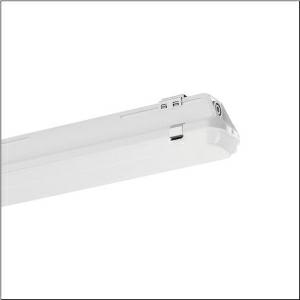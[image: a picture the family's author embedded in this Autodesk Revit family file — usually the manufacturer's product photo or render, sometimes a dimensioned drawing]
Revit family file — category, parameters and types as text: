
# Revit family: monsun_r__12_parking_51fg207p440h_4e28
name_source: partatom
category: Lighting Fixtures
units: mm (PartAtom-declared; Revit-internal decimal feet)

## family parameters
Cut with Voids When Loaded = No
Host = Face
Light Source = No
Part Type = Normal
Room Calculation Point = No
Round Connector Dimension = Use Diameter
Shared = No

## types (1)
- Monsun® 12 parking (1 x LED, 4820 lm, 29.2 W, 4000K)
    Apparent Load = 29 VA
    CIE Flux Codes = 45 75 93 94 100
    Color Rendering = 80
    Color Temperature = 4000K
    Default Elevation = 1800 mm
    Description = Monsun® 12 parking, damp-proof luminaire, chain hanger, primary optical cover: enclosure, of PC, light emission: direct distribution, primary light characteristic: symmetric, installation type: suspended mounting, surface-mounted, horizontal mounting, vertical mounting, LED rated luminous flux: 4.820 lm, light colour: 840, colour temperature: 4000K, control gear: ECG, with terminal, 3-pole, max. 2.5mm², mains connection: 220..240V, AC, 50/60Hz, rated input power: 29W, luminaire housing, of glass-fibre reinforced polyester, uncoated, bright grey, length: 1.590 mm, width: 90 mm, height: 88mm, clip for enclosure, of stainless steel (V2A), ceiling mounting element, of stainless steel (V2A), chain hanger, of stainless steel (V2A), protection rating (complete): IP66, insulation class (complete): insulation class I (protective earthing), certification: CE, ENEC, VDE, protection symbol: D, impact resistance: IK08, permissible ambient temperature for indoor applications: -35..+40°C, standard: EN 50419, EN 60598-2-1, no direct snow, no direct sun, no direct rain, for indoor or canopied outdoor use, corresponds to IFS (International Featured Standards) requirements for safety and quality in the food industry, packaging unit: 1 piece
    Height = 89 mm
    Lamp = 1 x LED
    Lamp Light Flux = 4820 lm
    Lamp Power = 29.2 W
    Lamp count = 1
    Length = 1590 mm
    Luminous efficacy = 165 lm/W
    Manufacturer = Siteco
    ModVariant = No
    Model = 51FG207P440H
    Mounting Place = Ceiling
    Mounting Type = Pendant
    Number of Poles = 1
    OnlyDefault = Yes
    Power Factor = 1
    Product Name = Monsun® 12 parking
    Product group = damp-proof luminaire | ceiling pendant
    ProductGroupID = 908
    Protection Class = Protection class I
    Protection Degree = IP 66
    RLX_Detail_Level = 1
    RlxData = <blob elided: 88473 chars, md5=a7c51cf6>
    Socket = socket
    Standby Power = 0 W
    System Light Flux = 4820 lm
    System Power = 29 W
    Type Comments = Product without accessories
    Type Image = l_1004748.jpg
    URL = http://relux.com
    VarID = ---
    Voltage = 0 V
    Weight = 0.00 kg
    Width = 90 mm

## geometry (parser evidence)
native form markers: Blend x4, Sweep x12
no freeform markers — native parametric forms only
